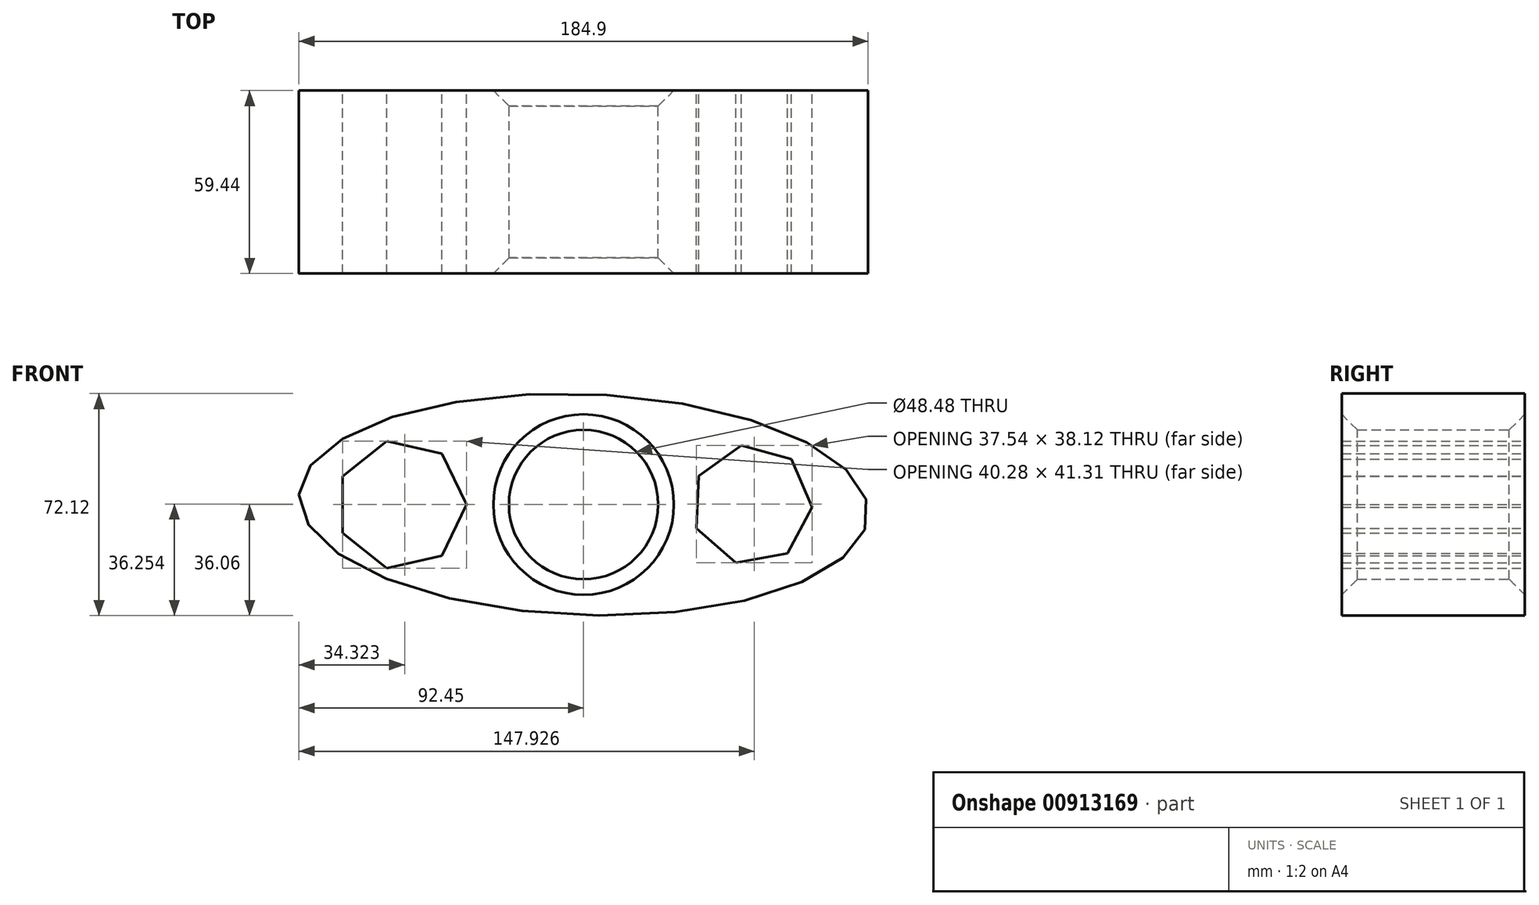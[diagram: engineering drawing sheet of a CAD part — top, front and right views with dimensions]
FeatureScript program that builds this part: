
annotation { "Feature Type Name" : "Feature", "Feature Type Description" : "" }
export const myFeature = defineFeature(function(context is Context, id is Id, definition is map)
    precondition{}
    {
        {
            var Q0;
            Q0=qCreatedBy(makeId("Front.planeOp"),FACE);
            var sketch = newSketch(context, id + "F0", { "sketchPlane" : qUnion([Q0])});
            skEllipse(sketch, "E0", {"center": v(0, 0) * mm, "majorRadius": 92.5 * mm, "minorRadius": 35.94 * mm, "majorAxis": v(-1, 0.03)});
            skCircle(sketch, "E1.cCircle", {"center": v(-59.18, 0) * mm, "radius": 19.09 * mm, "construction": true});
            skLineSegment(sketch, "E1.0", {"start": v(-78.27, -9.2) * mm, "end": v(-78.27, 9.2) * mm});
            skLineSegment(sketch, "E1.1", {"start": v(-78.27, 9.2) * mm, "end": v(-63.9, 20.66) * mm});
            skLineSegment(sketch, "E1.2", {"start": v(-63.9, 20.66) * mm, "end": v(-45.97, 16.57) * mm});
            skLineSegment(sketch, "E1.3", {"start": v(-45.97, 16.57) * mm, "end": v(-37.99, 0) * mm});
            skLineSegment(sketch, "E1.4", {"start": v(-37.99, 0) * mm, "end": v(-45.97, -16.57) * mm});
            skLineSegment(sketch, "E1.5", {"start": v(-45.97, -16.57) * mm, "end": v(-63.9, -20.66) * mm});
            skLineSegment(sketch, "E1.6", {"start": v(-63.9, -20.66) * mm, "end": v(-78.27, -9.2) * mm});
            skPoint(sketch, "E1.0.midPoint", {"position": v(-78.27, 0) * mm});
            skCircle(sketch, "E2.cCircle", {"center": v(54.7, 0) * mm, "radius": 17.63 * mm, "construction": true});
            skLineSegment(sketch, "E2.0", {"start": v(66.2, -15.83) * mm, "end": v(49.5, -18.87) * mm});
            skLineSegment(sketch, "E2.1", {"start": v(49.5, -18.87) * mm, "end": v(36.7, -7.7) * mm});
            skLineSegment(sketch, "E2.2", {"start": v(36.7, -7.7) * mm, "end": v(37.46, 9.27) * mm});
            skLineSegment(sketch, "E2.3", {"start": v(37.46, 9.27) * mm, "end": v(51.2, 19.25) * mm});
            skLineSegment(sketch, "E2.4", {"start": v(51.2, 19.25) * mm, "end": v(67.57, 14.74) * mm});
            skLineSegment(sketch, "E2.5", {"start": v(67.57, 14.74) * mm, "end": v(74.25, -0.87) * mm});
            skLineSegment(sketch, "E2.6", {"start": v(74.25, -0.87) * mm, "end": v(66.2, -15.83) * mm});
            skPoint(sketch, "E2.0.midPoint", {"position": v(57.85, -17.35) * mm});
            skCircle(sketch, "E3", {"center": v(0, 0) * mm, "radius": 24.24 * mm});
            skSolve(sketch);
        }
        {
            var Q0;
            Q0 = qSketchRegion(id + "F0", true);
            extrude(context, id + "F1", {"entities" : qUnion([Q0]), "depth" : 59.44 * mm, "offsetDistance" : 25.4 * mm});
        }
        {
            var Q0;
            Q0=makeQuery(id+"F1.opExtrude","CAP_EDGE",EDGE,{"disambiguationData":[OSD([sQuery(id+"F0.wireOp",EDGE,"E3")])],"isStart":false});
            var Q1;
            Q1=makeQuery(id+"F1.opExtrude","CAP_EDGE",EDGE,{"disambiguationData":[OSD([sQuery(id+"F0.wireOp",EDGE,"E3")])],"isStart":true});
            chamfer(context, id + "F2", {"entities" : qUnion([Q0, Q1]), "width" : 5.08 * mm, "tangentPropagation" : true});
        }
    });
